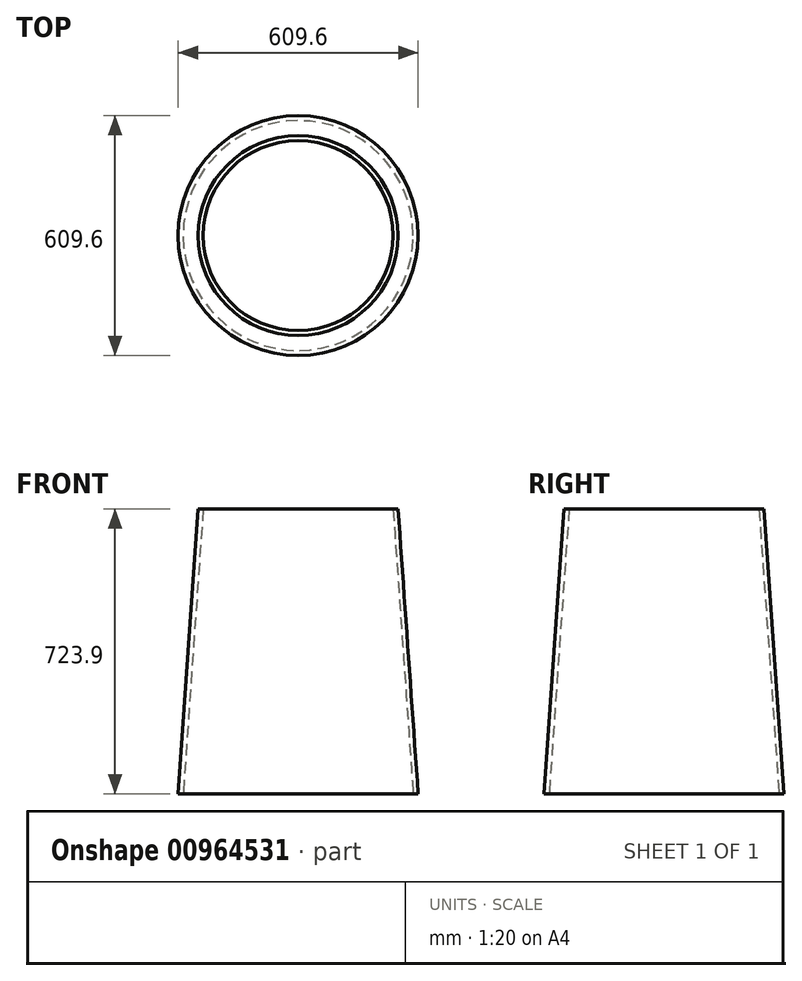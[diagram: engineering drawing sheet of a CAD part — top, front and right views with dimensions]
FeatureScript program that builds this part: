
annotation { "Feature Type Name" : "Feature", "Feature Type Description" : "" }
export const myFeature = defineFeature(function(context is Context, id is Id, definition is map)
    precondition{}
    {
        {
            var Q0;
            Q0=qCreatedBy(makeId("Front.planeOp"),FACE);
            var sketch = newSketch(context, id + "F0", { "sketchPlane" : qUnion([Q0])});
            skLineSegment(sketch, "E0", {"start": v(292.1, 0) * mm, "end": v(304.8, 0) * mm});
            skLineSegment(sketch, "E1", {"start": v(304.8, 0) * mm, "end": v(254, 723.9) * mm});
            skLineSegment(sketch, "E2", {"start": v(254, 723.9) * mm, "end": v(241.3, 723.9) * mm});
            skLineSegment(sketch, "E3", {"start": v(241.3, 723.9) * mm, "end": v(292.1, 0) * mm});
            skLineSegment(sketch, "E4", {"start": v(0, 568.36) * mm, "end": v(0, 0) * mm});
            skSolve(sketch);
        }
        {
            var Q0;
            Q0 = qSketchRegion(id + "F0", true);
            var Q1;
            Q1=sQuery(id+"F0.wireOp",EDGE,"E4");
            revolve(context, id + "F1", {"surfaceOperationType" : NewSurfaceOperationType.NEW, "entities" : qUnion([Q0]), "axis" : qUnion([Q1]), "revolveType" : RevolveType.FULL});
        }
    });
